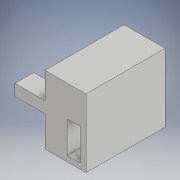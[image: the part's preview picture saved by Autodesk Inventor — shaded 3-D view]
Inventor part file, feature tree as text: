
AUTODESK INVENTOR PART (.ipt)
format: ipt  version: 2017 (Build 210142000, 142)  size: 116,736 bytes
history: native  units: in
note: dims shown in document units (in); Inventor stores cm internally (conversion verified against a paired STEP export)
features: extrude x3, sketch x3, projected_geometry x2
ambient origin geometry x8: Origin, YZ Plane, XZ Plane, XY Plane, X Axis, Y Axis, Z Axis, Center Point
bodies: Solid1 (feature_tree)
feature tree (8):
  extrude  "Extrusion1"  Depth=5.44in
  extrude  "Extrusion2"  Depth=0.75in
  extrude  "Extrusion3"  Depth=0.75in
  sketch  "Sketch1"  dims[d0=9.063in d1=5.44in]
  sketch  "Sketch2"  dims[d2=10.5in d3=0.0in d4=0.75in]
  projected_geometry  "Projected Loop1"
  sketch  "Sketch3"  dims[d5=2.5in d7=0.75in d8=10.5in d9=0.0in d10=4.95in d11=4.0in d12=1.5in d14=5.0in d15=2.5in d16=0.0in]
  projected_geometry  "Projected Loop2"
